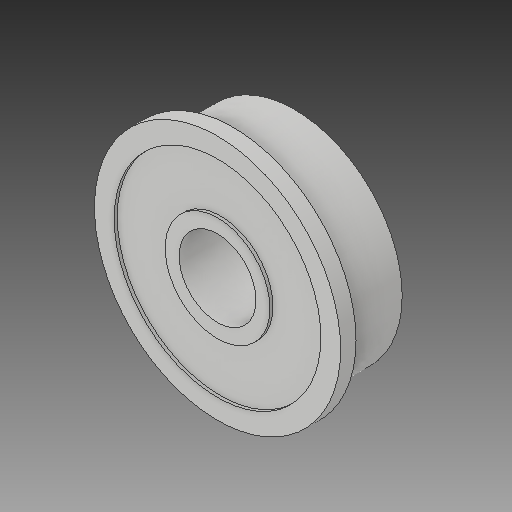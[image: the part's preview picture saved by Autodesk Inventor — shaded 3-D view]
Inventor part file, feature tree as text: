
AUTODESK INVENTOR PART (.ipt)
format: ipt  version: 2018 (Build 220112000, 112)  size: 153,088 bytes
history: native  units: mm
features: other x5, extrude x3, sketch x3, reference x2
ambient origin geometry x8: Origin, YZ Plane, XZ Plane, XY Plane, X Axis, Y Axis, Z Axis, Center Point
bodies: Solid1 (feature_tree)
feature tree (13):
  extrude  "Extrusion1"  Depth=5.0mm
  extrude  "Extrusion2"  Depth=5.0mm
  extrude  "Extrusion3"  Depth=0.2mm TaperAngle=0.0deg
  sketch  "Sketch1"  dims[d0=5.0mm d1=14.0mm]
  reference  "Reference1"
  sketch  "Sketch2"  dims[d2=5.0mm d3=0.0mm d4=16.0mm]
  sketch  "Sketch3"  dims[d5=1.0mm d6=0.0mm d7=0.2mm d8=0.0mm]
  reference  "Reference2"
  other  "<userpath>\OneDrive\SL-Inventor\SL-Beast 3D Printer\x-aXIS-aSSEMBLY.iam"
  other  "x-aXIS-aSSEMBLY.iam"
  other  "Washer:1"
  parser-record x1  (decoder bookkeeping rows leaked as tree rows — omitted from the tree; the rows remain in map.json)
  other  "Forged Socket Head Cap Screw - Metric M5x0.8 x 25:1"
note: 1 file-system path scrubbed to <path> (originals preserved in map.json)
